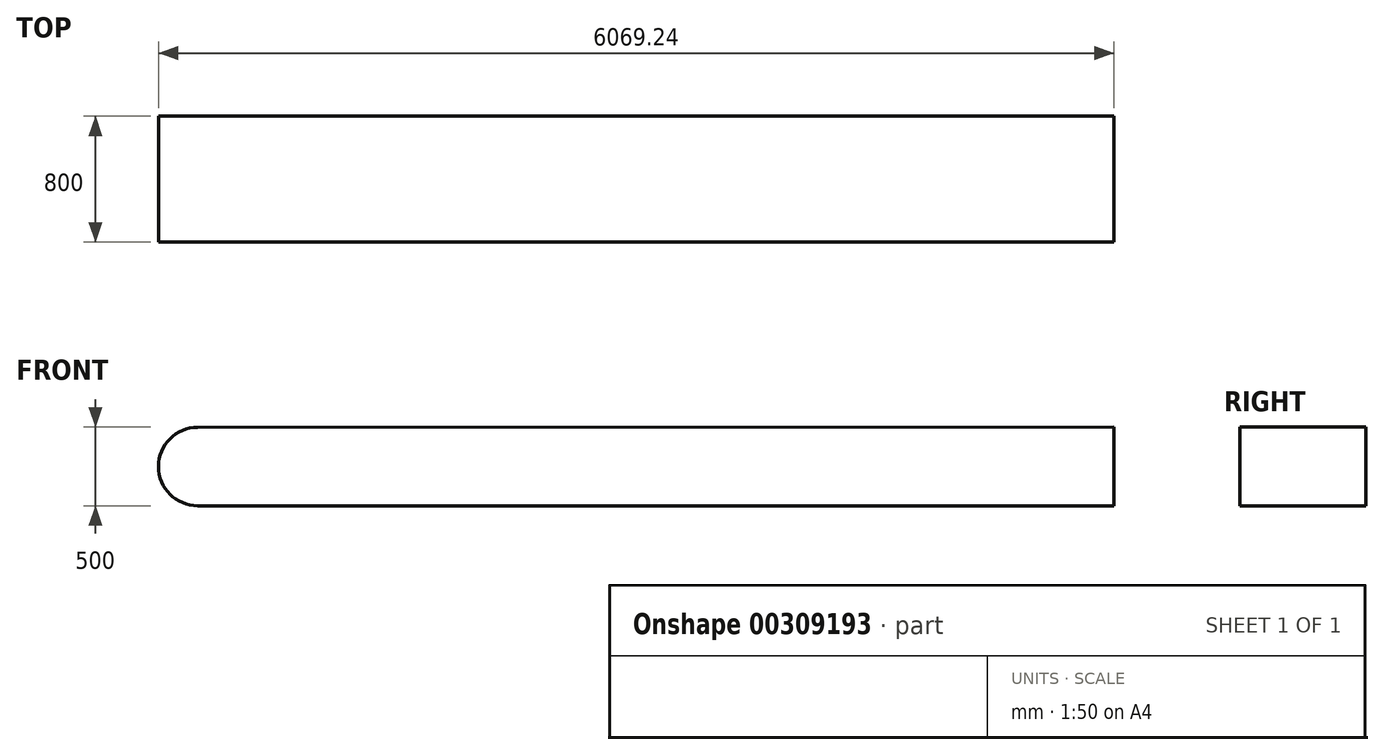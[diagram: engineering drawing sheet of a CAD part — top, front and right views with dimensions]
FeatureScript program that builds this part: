
annotation { "Feature Type Name" : "Feature", "Feature Type Description" : "" }
export const myFeature = defineFeature(function(context is Context, id is Id, definition is map)
    precondition{}
    {
        {
            var Q0;
            Q0=qCreatedBy(makeId("Front.planeOp"),FACE);
            var sketch = newSketch(context, id + "F0", { "sketchPlane" : qUnion([Q0])});
            skLineSegment(sketch, "E0", {"start": v(-1499.32, 287.89) * mm, "end": v(4320.68, 289.41) * mm});
            skLineSegment(sketch, "E1", {"start": v(4320.68, 289.41) * mm, "end": v(4320.68, -210.59) * mm});
            skLineSegment(sketch, "E2", {"start": v(4320.68, -210.59) * mm, "end": v(-1499.32, -210.59) * mm});
            skArc(sketch, "E3", {"start": v(-1499.32, 287.89) * mm, "mid": v(-1748.56, 38.65) * mm, "end": v(-1499.32, -210.59) * mm});
            skLineSegment(sketch, "E4", {"start": v(-1499.32, 287.89) * mm, "end": v(-1499.32, -210.59) * mm, "construction": true});
            skSolve(sketch);
        }
        {
            var Q0;
            Q0 = qSketchRegion(id + "F0", true);
            extrude(context, id + "F1", {"entities" : qUnion([Q0]), "depth" : 800 * mm});
        }
    });
